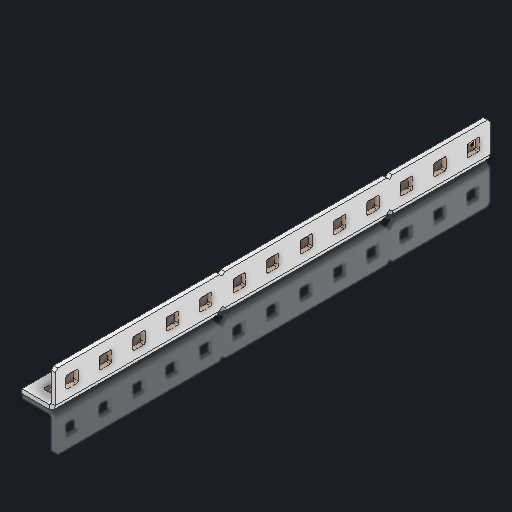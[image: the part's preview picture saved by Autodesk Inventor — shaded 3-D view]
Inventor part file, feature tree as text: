
AUTODESK INVENTOR PART (.ipt)
format: ipt  version: 2023.2 (Build 272271030, 271C)  size: 565,248 bytes
history: native  units: in
note: dims shown in document units (in); Inventor stores cm internally (conversion verified against a paired STEP export)
features: other x31, extrude x25, sheet_metal_op x10, sketch x8, mirror x1, pattern_linear x1, chamfer x1
ambient origin geometry x8: Origin, YZ Plane, XZ Plane, XY Plane, X Axis, Y Axis, Z Axis, Center Point
bodies: Solid1 (feature_tree), Body (feature_tree)
feature tree (77):
  other  "Flange Pattern Plane"
  sheet_metal_op  "Flange Pattern"
  sheet_metal_op  "Body Pattern"
  other  "Arc Length"
  mirror  "Notch Mirror"
  pattern_linear  "Notch Pattern"  Spacing1=0.25in  [1 undecoded]
  chamfer  "End Chamfer"
  extrude  "Half Cut"  Depth=0.0625in
  sketch  "Sketch1"  dims[d0=1.5in]
  other  "Plate1"
  sketch  "Sketch2"  dims[d1=6.5in]
  other  "Plate2"
  sheet_metal_op  "Bend1"
  sheet_metal_op  "Corner1"
  sketch  "Sketch3"  dims[d2=0.0625in]
  other  "Flange Pattern Sketch"
  sketch  "Sketch7"  dims[d3=0.0625in]
  other  "Srf1"
  other  "Srf2"
  sketch  "Sketch8"  dims[d4=0.0312in]
  sketch  "Sketch9"  dims[d5=0.125in]
  other  "Srf91"
  sheet_metal_op  "Body Pattern Sketch"
  other  "Srf92"
  sketch  "Sketch13"  dims[d6=0.0625in]
  sketch  "Sketch14"  dims[d7=0.5in d8=90.0deg d9=0.0312in d10=0.25in d11=0.0625in d12=0.0625in d16=0.182in d17=0.02in d18=0.0625in d19=0.0in d20=0.25in d21=0.25in d46=0.172in d47=1.0in d48=0.0in d49=0.182in d50=0.02in d51=0.25in d52=0.25in d53=0.0625in d54=0.0in d55=0.172in d56=1.0in d57=0.0in d60=5.1181in d62=0.5in d63=0.3937in d65=0.5in d85=0.1473in d86=0.1782in d88=0.04in d89=0.0625in d90=0.0in d91=0.04in d92=0.0491in d95=2.5in d96=0.04in d97=0.25in d98=45.0deg d101=0.0in d102=2.497in d131=0.5in d132=5.1181in d134=0.5in d139=0.5in]
  other  "Srf856"
  other  "Srf1310"
  other  "Srf1311"
  other  "Srf1312"
  other  "Srf1376"
  other  "Srf1377"
  other  "Srf1728"
  other  "Srf1755"
  other  "Srf1878"
  other  "Srf1879"
  other  "Srf1880"
  other  "Srf1881"
  other  "Srf1882"
  other  "Srf1883"
  other  "Srf1884"
  other  "Srf1942"
  other  "Srf1943"
  other  "Srf1944"
  other  "Srf1945"
  other  "Srf1946"
  other  "Srf1947"
  other  "Srf1948"
  sheet_metal_op  "Flange Stamp"
  sheet_metal_op  "Flange Circle"
  sheet_metal_op  "Body Stamp"
  sheet_metal_op  "Body Circle"
  sheet_metal_op  "Notch"
  extrude  "ExtrusionSrf2"  Depth=0.0625in
  extrude  "ExtrusionSrf92"  Depth=0.5in
  extrude  "ExtrusionSrf856"  Depth=0.02in
  extrude  "ExtrusionSrf1310"  Depth=0.0625in
  extrude  "ExtrusionSrf1311"  TaperAngle=0.0deg  [1 undecoded]
  extrude  "ExtrusionSrf1312"  Depth=0.5in
  extrude  "ExtrusionSrf1376"  Depth=0.5in
  extrude  "ExtrusionSrf1377"  Depth=0.5in
  extrude  "ExtrusionSrf1728"  Depth=0.5in TaperAngle=0.0deg
  extrude  "ExtrusionSrf1755"  Depth=0.5in
  extrude  "ExtrusionSrf1878"  Depth=0.02in
  extrude  "ExtrusionSrf1879"  Depth=0.5in
  extrude  "ExtrusionSrf1880"  Depth=0.5in
  extrude  "ExtrusionSrf1881"  Depth=0.0625in
  extrude  "ExtrusionSrf1882"  TaperAngle=0.0deg  [1 undecoded]
  extrude  "ExtrusionSrf1883"  Depth=0.5in
  extrude  "ExtrusionSrf1884"  Depth=0.5in TaperAngle=0.0deg
  extrude  "ExtrusionSrf1942"  Depth=0.5in
  extrude  "ExtrusionSrf1943"  Depth=0.5in
  extrude  "ExtrusionSrf1944"  Depth=0.5in
  extrude  "ExtrusionSrf1945"  Depth=0.5in
  extrude  "ExtrusionSrf1946"  Depth=0.5in
  extrude  "ExtrusionSrf1947"  Depth=0.0625in
  extrude  "ExtrusionSrf1948"  TaperAngle=0.0deg  [1 undecoded]
note: 4 required parameter values undecoded (feature->parameter linkage not recoverable at this tier; creation-order binding heuristic only, values carry confidence <= 0.55)
